# Revit family: Dynamic Fenestration - Lift & Slide - OX HXP Sill
name_source: partatom
category: Doors
units: mm (PartAtom-declared; Revit-internal decimal feet)

## family parameters
Always vertical = Yes
Cut with Voids When Loaded = No
Host = Wall
OmniClass Number = 23.30.20.00
OmniClass Title = Windows
Room Calculation Point = No
Shared = No

## types (1)
- 190" x 132"
    Analytic Construction = <None>
    Default Sill Height = 10"
    Define Thermal Properties by = Schematic Type
    Description = Lift & Slide - OX HXP Sill
    Frame Material = Arte Metal
    Gap Fill = Argon
    Glass Material = Glass
    Glass Type = Triple Silve LowE / Clear
    Handle Height = 50"
    Height = 127 1/2"
    Manufacturer = Dynamic Fenestration
    Max. Height = 132"
    Max. Width = 190"
    Min. Height = 48"
    Min. Width = 60"
    Model = Lift & Slide
    Rough Height = 132"
    Rough Width = 190"
    Rubber Material = Rubber
    Thickness = 6 1/2"
    Wall Closure = By host
    Width = 95 1/2"
    Wood Material = Wood

## geometry (parser evidence)
native form markers: Sweep x32
no freeform markers — native parametric forms only
